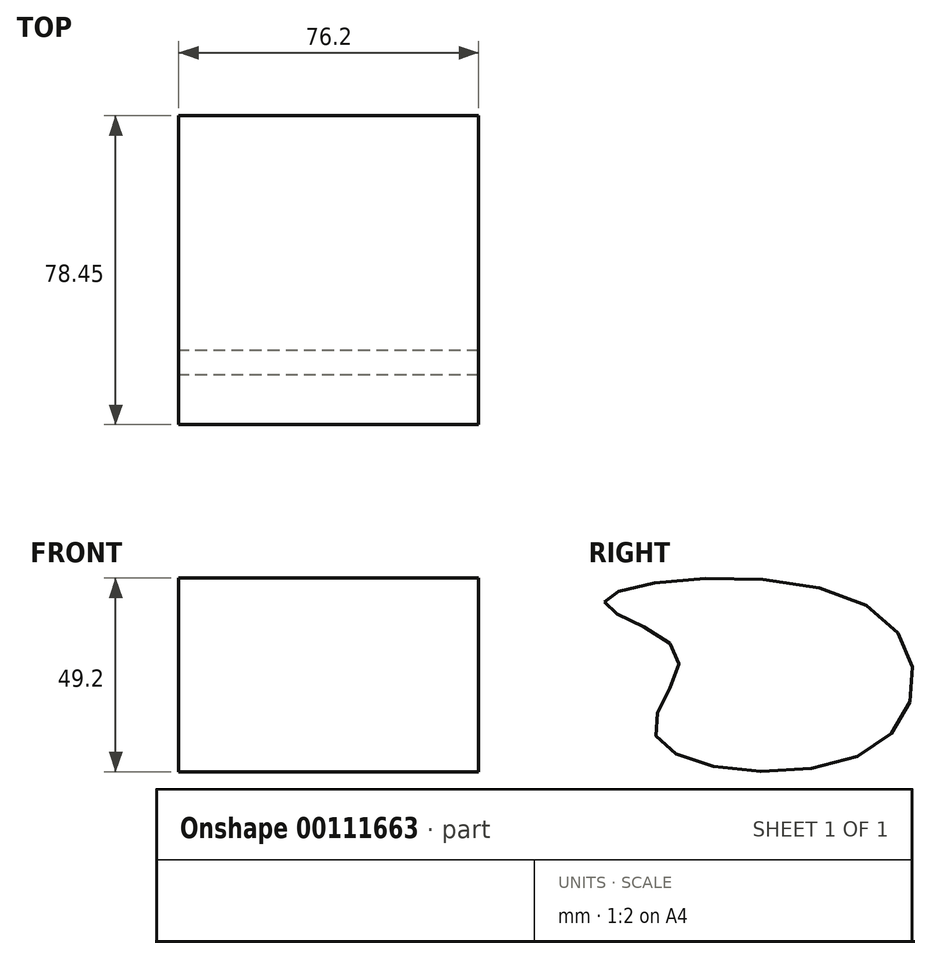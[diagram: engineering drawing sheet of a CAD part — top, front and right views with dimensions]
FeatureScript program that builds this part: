
annotation { "Feature Type Name" : "Feature", "Feature Type Description" : "" }
export const myFeature = defineFeature(function(context is Context, id is Id, definition is map)
    precondition{}
    {
        {
            var Q0;
            Q0=qCreatedBy(makeId("Right.planeOp"),FACE);
            var sketch = newSketch(context, id + "F0", { "sketchPlane" : qUnion([Q0])});
            skFitSpline(sketch, "E0", {"points": [v(-26.96, 36.5) * mm, v(40.44, 35.14) * mm, v(42.17, 0) * mm, v(-14.06, 2.8) * mm, v(-8.47, 23.4) * mm, v(-26.96, 36.5) * mm]});
            skSolve(sketch);
        }
        {
            var Q0;
            Q0 = qSketchRegion(id + "F0", true);
            extrude(context, id + "F1", {"entities" : qUnion([Q0]), "depth" : 76.2 * mm});
        }
    });
